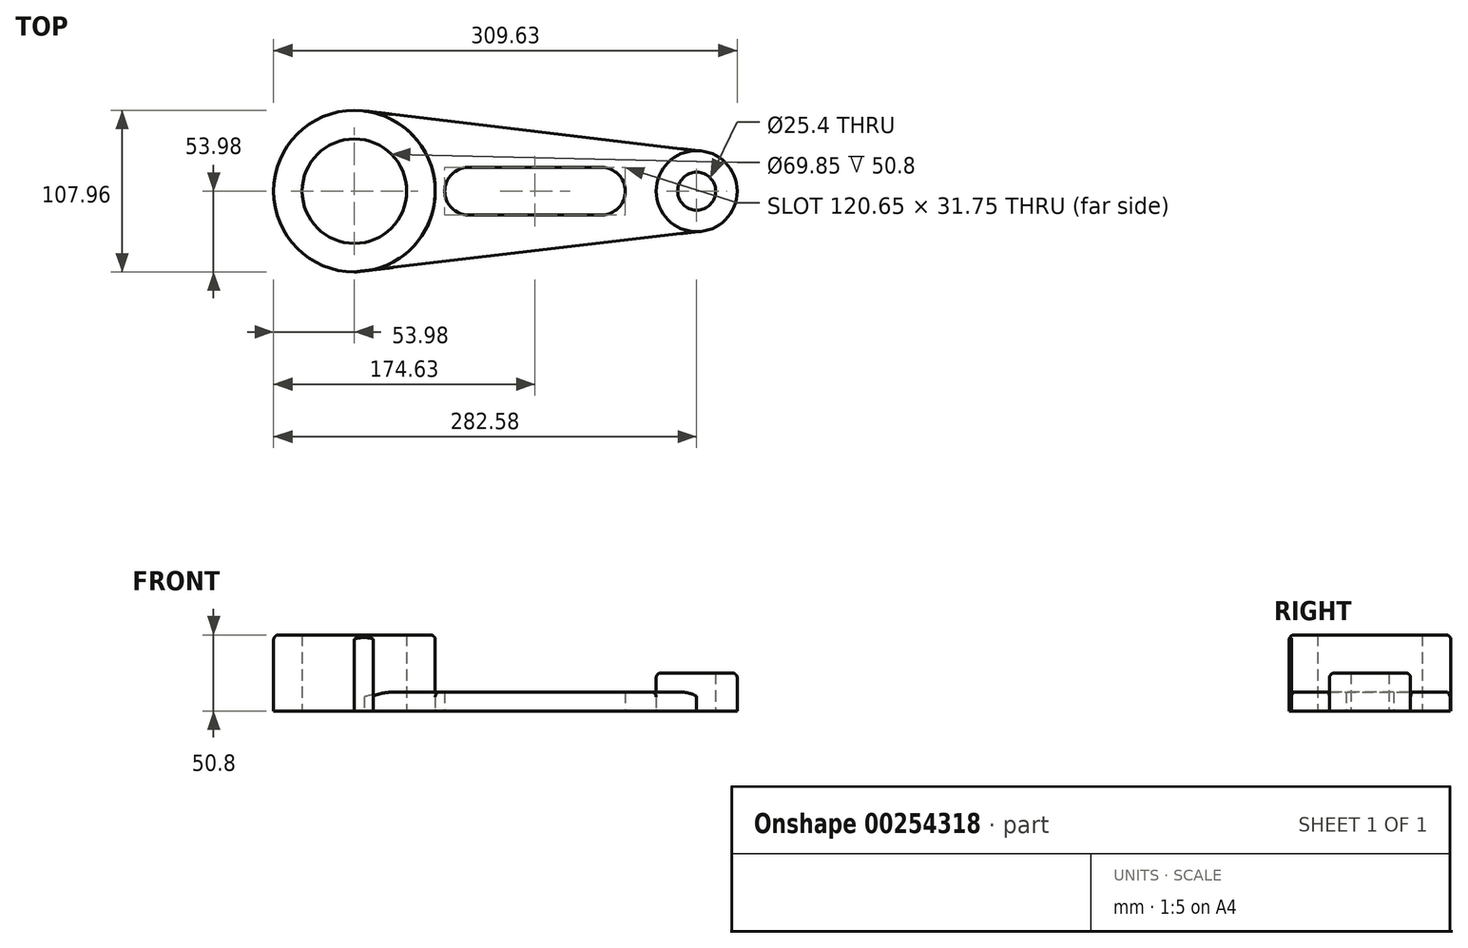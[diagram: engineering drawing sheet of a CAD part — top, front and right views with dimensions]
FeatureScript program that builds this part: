
annotation { "Feature Type Name" : "Feature", "Feature Type Description" : "" }
export const myFeature = defineFeature(function(context is Context, id is Id, definition is map)
    precondition{}
    {
        {
            var Q0;
            Q0=qCreatedBy(makeId("Top.planeOp"),FACE);
            var sketch = newSketch(context, id + "F0", { "sketchPlane" : qUnion([Q0])});
            skCircle(sketch, "E0", {"center": v(-76.2, 0) * mm, "radius": 34.93 * mm});
            skCircle(sketch, "E1", {"center": v(-76.2, 0) * mm, "radius": 53.98 * mm});
            skCircle(sketch, "E2", {"center": v(152.4, 0) * mm, "radius": 12.7 * mm});
            skCircle(sketch, "E3", {"center": v(152.4, 0) * mm, "radius": 27.05 * mm});
            skLineSegment(sketch, "E4", {"start": v(-76.2, -53.98) * mm, "end": v(152.4, -27.05) * mm});
            skLineSegment(sketch, "E5", {"start": v(152.4, -12.7) * mm, "end": v(152.4, 12.7) * mm});
            skLineSegment(sketch, "E6", {"start": v(152.4, 27.05) * mm, "end": v(-76.2, 54.36) * mm});
            skLineSegment(sketch, "E7", {"start": v(-76.2, 54.36) * mm, "end": v(-76.2, 53.97) * mm});
            skLineSegment(sketch, "E8", {"start": v(-76.2, 0) * mm, "end": v(152.4, 0) * mm});
            skLineSegment(sketch, "E9", {"start": v(0, -15.88) * mm, "end": v(88.9, -15.88) * mm});
            skLineSegment(sketch, "E10", {"start": v(88.9, 15.88) * mm, "end": v(0, 15.88) * mm});
            skArc(sketch, "E11", {"start": v(0, 15.88) * mm, "mid": v(-15.88, 0) * mm, "end": v(0, -15.88) * mm});
            skArc(sketch, "E12", {"start": v(88.9, 15.88) * mm, "mid": v(104.78, 0) * mm, "end": v(88.9, -15.88) * mm});
            skLineSegment(sketch, "E13.trimOffspring", {"start": v(-76.2, 34.92) * mm, "end": v(-76.2, -34.93) * mm});
            skSolve(sketch);
        }
        {
            var Q0;
            {var subQ0=sQuery(id+"F0.wireOp",EDGE,"E7");var subQ1=sQuery(id+"F0.wireOp",EDGE,"E0");var subQ2=makeQuery(id+"F0.imprint","INTERSECT",VERTEX,{"disambiguationData":[OD(0.0)],"derivedFrom":[subQ1,subQ0]});Q0=makeQuery(id+"F0.imprint","IMPRINT",FACE,{"disambiguationData":[TD([[makeQuery(id+"F0.imprint","IMPRINT",EDGE,{"disambiguationData":[TD([[subQ2,-1.0]])],"derivedFrom":subQ1}),-1.0]])]});}
            var Q1;
            {var subQ2=sQuery(id+"F0.wireOp",EDGE,"E7");var subQ4=sQuery(id+"F0.wireOp",EDGE,"E0");var subQ5=makeQuery(id+"F0.imprint","INTERSECT",VERTEX,{"disambiguationData":[OD(0.0)],"derivedFrom":[subQ4,subQ2]});Q1=makeQuery(id+"F0.imprint","IMPRINT",FACE,{"disambiguationData":[TD([[makeQuery(id+"F0.imprint","IMPRINT",EDGE,{"disambiguationData":[TD([[subQ5,1.0]])],"derivedFrom":subQ4}),-1.0]])]});}
            var Q2;
            {var subQ4=sQuery(id+"F0.wireOp",EDGE,"E0");var subQ7=sQuery(id+"F0.wireOp",EDGE,"E8");var subQ9=makeQuery(id+"F0.imprint","INTERSECT",VERTEX,{"derivedFrom":[subQ4,subQ7]});Q2=makeQuery(id+"F0.imprint","IMPRINT",FACE,{"disambiguationData":[TD([[makeQuery(id+"F0.imprint","IMPRINT",EDGE,{"disambiguationData":[TD([[subQ9,1.0]])],"derivedFrom":subQ4}),-1.0]])]});}
            extrude(context, id + "F1", {"entities" : qUnion([Q0, Q1, Q2]), "depth" : 50.8 * mm});
        }
        {
            var Q0;
            {var subQ0=sQuery(id+"F0.wireOp",EDGE,"E8");var subQ1=sQuery(id+"F0.wireOp",EDGE,"E2");var subQ2=makeQuery(id+"F0.imprint","INTERSECT",VERTEX,{"derivedFrom":[subQ1,subQ0]});Q0=makeQuery(id+"F0.imprint","IMPRINT",FACE,{"disambiguationData":[TD([[makeQuery(id+"F0.imprint","IMPRINT",EDGE,{"disambiguationData":[TD([[subQ2,1.0]])],"derivedFrom":subQ1}),-1.0]])]});}
            var Q1;
            {var subQ0=sQuery(id+"F0.wireOp",EDGE,"E5");var subQ1=sQuery(id+"F0.wireOp",EDGE,"E2");var subQ2=makeQuery(id+"F0.imprint","INTERSECT",VERTEX,{"disambiguationData":[OD(0.0)],"derivedFrom":[subQ1,subQ0]});Q1=makeQuery(id+"F0.imprint","IMPRINT",FACE,{"disambiguationData":[TD([[makeQuery(id+"F0.imprint","IMPRINT",EDGE,{"disambiguationData":[TD([[subQ2,1.0]])],"derivedFrom":subQ1}),-1.0]])]});}
            var Q2;
            {var subQ0=sQuery(id+"F0.wireOp",EDGE,"E8");var subQ1=sQuery(id+"F0.wireOp",EDGE,"E2");var subQ2=makeQuery(id+"F0.imprint","INTERSECT",VERTEX,{"derivedFrom":[subQ1,subQ0]});Q2=makeQuery(id+"F0.imprint","IMPRINT",FACE,{"disambiguationData":[TD([[makeQuery(id+"F0.imprint","IMPRINT",EDGE,{"disambiguationData":[TD([[subQ2,-1.0]])],"derivedFrom":subQ1}),-1.0]])]});}
            extrude(context, id + "F2", {"entities" : qUnion([Q0, Q1, Q2]), "depth" : 25.4 * mm});
        }
        {
            var Q0;
            {var subQ12=sQuery(id+"F0.wireOp",EDGE,"E10");Q0=makeQuery(id+"F0.imprint","IMPRINT",FACE,{"disambiguationData":[TD([[makeQuery(id+"F0.imprint","IMPRINT",EDGE,{"derivedFrom":subQ12}),-1.0]])]});}
            var Q1;
            {var subQ12=sQuery(id+"F0.wireOp",EDGE,"E9");Q1=makeQuery(id+"F0.imprint","IMPRINT",FACE,{"disambiguationData":[TD([[makeQuery(id+"F0.imprint","IMPRINT",EDGE,{"derivedFrom":subQ12}),-1.0]])]});}
            extrude(context, id + "F3", {"entities" : qUnion([Q0, Q1]), "depth" : 12.7 * mm});
        }
        {
            var Q0;
            Q0=makeQuery(id+"F3.opExtrude","CAP_EDGE",EDGE,{"disambiguationData":[OSD([sQuery(id+"F0.wireOp",EDGE,"E1")])],"isStart":false});
            fillet(context, id + "F4", {"entities" : qUnion([Q0]), "radius" : 3.17 * mm, "tangentPropagation" : true, "allowEdgeOverflow" : false});
        }
        {
            var Q0;
            Q0=makeQuery(id+"F3.opExtrude","CAP_EDGE",EDGE,{"disambiguationData":[OSD([sQuery(id+"F0.wireOp",EDGE,"E3")])],"isStart":false});
            fillet(context, id + "F5", {"entities" : qUnion([Q0]), "radius" : 3.17 * mm, "tangentPropagation" : true, "allowEdgeOverflow" : false});
        }
        {
            var Q0;
            Q0=makeQuery(id+"F1.opExtrude","CAP_EDGE",EDGE,{"disambiguationData":[OSD([sQuery(id+"F0.wireOp",EDGE,"E1")])],"isStart":false});
            var Q1;
            Q1=makeQuery(id+"F2.opExtrude","CAP_EDGE",EDGE,{"disambiguationData":[OSD([sQuery(id+"F0.wireOp",EDGE,"E3")])],"isStart":false});
            fillet(context, id + "F6", {"entities" : qUnion([Q0, Q1]), "radius" : 3.17 * mm, "tangentPropagation" : true, "allowEdgeOverflow" : false});
        }
    });
